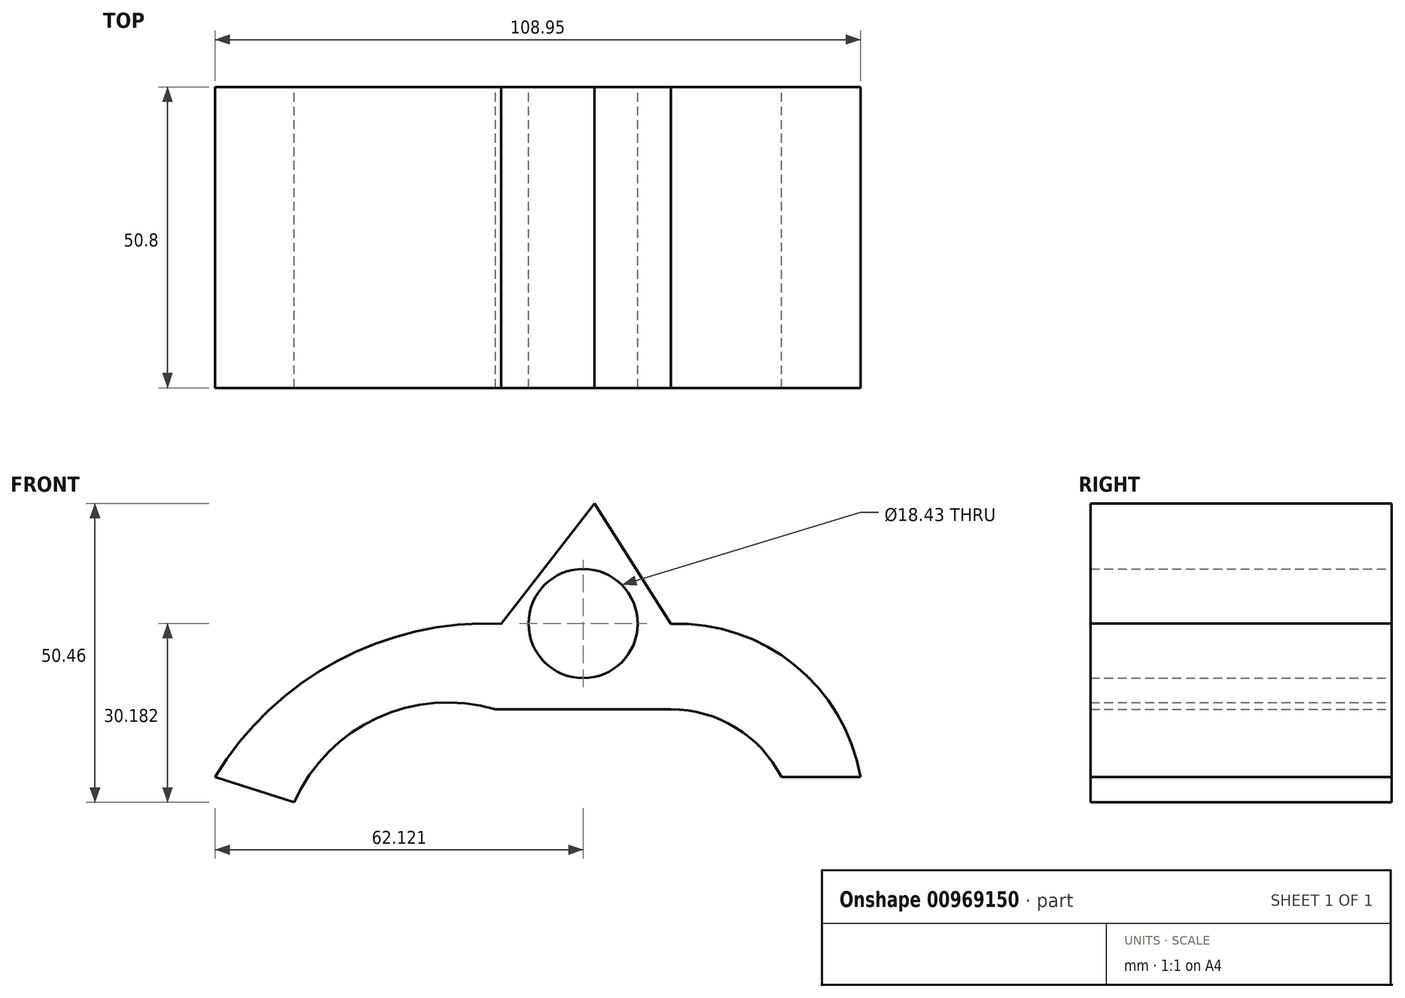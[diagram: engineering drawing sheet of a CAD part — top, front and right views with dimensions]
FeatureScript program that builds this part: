
annotation { "Feature Type Name" : "Feature", "Feature Type Description" : "" }
export const myFeature = defineFeature(function(context is Context, id is Id, definition is map)
    precondition{}
    {
        {
            var Q0;
            Q0=qCreatedBy(makeId("Front.planeOp"),FACE);
            var sketch = newSketch(context, id + "F0", { "sketchPlane" : qUnion([Q0])});
            skArc(sketch, "E0", {"start": v(-7.53, 14.43) * mm, "mid": v(-35.21, 8.13) * mm, "end": v(-55.79, -11.45) * mm});
            skArc(sketch, "E1", {"start": v(53.16, -11.45) * mm, "mid": v(41.99, 7.48) * mm, "end": v(21.14, 14.43) * mm});
            skLineSegment(sketch, "E2", {"start": v(-7.53, 14.43) * mm, "end": v(8.24, 34.75) * mm});
            skLineSegment(sketch, "E3", {"start": v(21.14, 14.43) * mm, "end": v(8.24, 34.75) * mm});
            skLineSegment(sketch, "E4", {"start": v(-55.79, -11.45) * mm, "end": v(-42.4, -15.7) * mm});
            skArc(sketch, "E5", {"start": v(-8.48, 0) * mm, "mid": v(-28.41, -1.45) * mm, "end": v(-42.4, -15.7) * mm});
            skLineSegment(sketch, "E6", {"start": v(-8.48, 0) * mm, "end": v(21.14, 0) * mm});
            skArc(sketch, "E7", {"start": v(39.78, -11.45) * mm, "mid": v(32.08, -3.09) * mm, "end": v(21.14, 0) * mm});
            skLineSegment(sketch, "E8", {"start": v(39.78, -11.45) * mm, "end": v(53.16, -11.45) * mm});
            skCircle(sketch, "E9", {"center": v(6.33, 14.47) * mm, "radius": 9.22 * mm});
            skPoint(sketch, "E9.centerSnap0", {"position": v(6.33, 0) * mm});
            skSolve(sketch);
        }
        {
            var Q0;
            Q0=makeQuery(id+"F0.imprint","IMPRINT",FACE,{"disambiguationData":[TD([[makeQuery(id+"F0.imprint","IMPRINT",EDGE,{"derivedFrom":sQuery(id+"F0.wireOp",EDGE,"E0")}),1.0]])]});
            extrude(context, id + "F1", {"entities" : qUnion([Q0]), "depth" : 25.4 * mm, "offsetDistance" : 25.4 * mm});
        }
        {
            var Q0;
            Q0=makeQuery(id+"F1.opExtrude","CAP_FACE",FACE,{"disambiguationData":[OSD([sQuery(id+"F0.wireOp",EDGE,"E0"),sQuery(id+"F0.wireOp",EDGE,"E1"),sQuery(id+"F0.wireOp",EDGE,"E2"),sQuery(id+"F0.wireOp",EDGE,"E3"),sQuery(id+"F0.wireOp",EDGE,"E4"),sQuery(id+"F0.wireOp",EDGE,"E5"),sQuery(id+"F0.wireOp",EDGE,"E6"),sQuery(id+"F0.wireOp",EDGE,"E7"),sQuery(id+"F0.wireOp",EDGE,"E8"),sQuery(id+"F0.wireOp",EDGE,"E9")])],"isStart":false});
            extrude(context, id + "F2", {"entities" : qUnion([Q0]), "operationType" : NewBodyOperationType.ADD, "depth" : 25.4 * mm, "offsetDistance" : 25.4 * mm});
        }
    });
